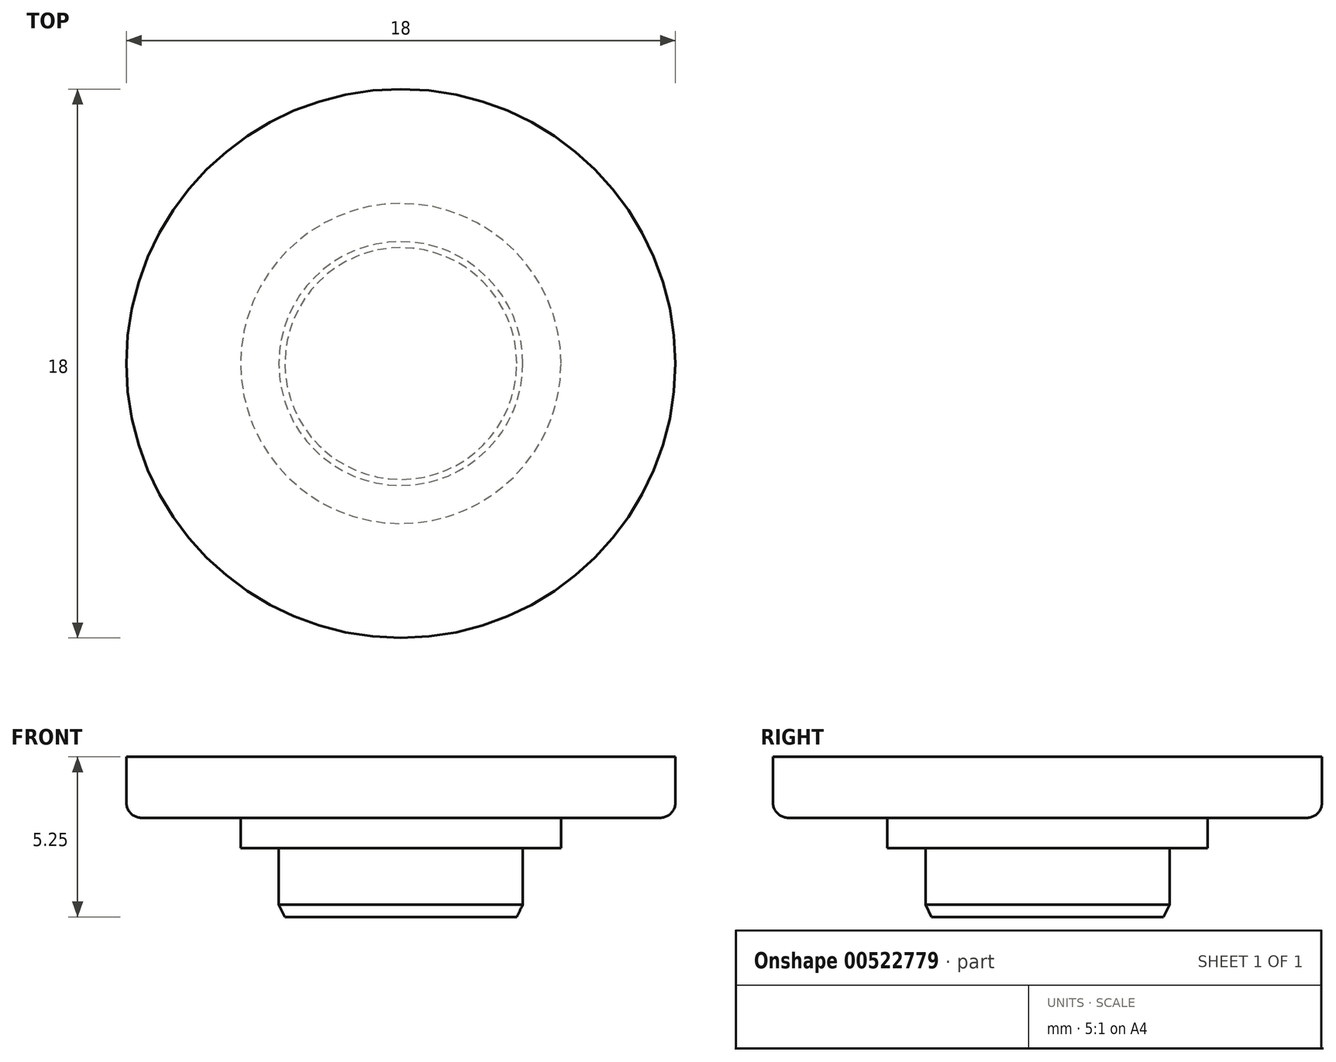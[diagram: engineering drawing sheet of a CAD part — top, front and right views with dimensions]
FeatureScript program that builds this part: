
annotation { "Feature Type Name" : "Feature", "Feature Type Description" : "" }
export const myFeature = defineFeature(function(context is Context, id is Id, definition is map)
    precondition{}
    {
        {
            var Q0;
            Q0=qCreatedBy(makeId("Front.planeOp"),FACE);
            var sketch = newSketch(context, id + "F0", { "sketchPlane" : qUnion([Q0])});
            skLineSegment(sketch, "E0", {"start": v(0, 31.24) * mm, "end": v(0, -31.24) * mm});
            skLineSegment(sketch, "E1", {"start": v(0, -3.25) * mm, "end": v(-4, -3.25) * mm});
            skLineSegment(sketch, "E2", {"start": v(-4, -3.25) * mm, "end": v(-4, -1) * mm});
            skLineSegment(sketch, "E3", {"start": v(-4, -1) * mm, "end": v(-5.25, -1) * mm});
            skLineSegment(sketch, "E4", {"start": v(-5.25, -1) * mm, "end": v(-5.25, 0) * mm});
            skLineSegment(sketch, "E5", {"start": v(-5.25, 0) * mm, "end": v(-9, 0) * mm});
            skLineSegment(sketch, "E6", {"start": v(-9, 0) * mm, "end": v(-9, 2) * mm});
            skLineSegment(sketch, "E7", {"start": v(-9, 2) * mm, "end": v(0, 2) * mm});
            skLineSegment(sketch, "E8", {"start": v(0, 2) * mm, "end": v(0, -3.25) * mm});
            skSolve(sketch);
        }
        {
            var Q0;
            Q0=makeQuery(id+"F0.imprint","IMPRINT",FACE,{"disambiguationData":[TD([[makeQuery(id+"F0.imprint","IMPRINT",EDGE,{"derivedFrom":sQuery(id+"F0.wireOp",EDGE,"E1")}),-1.0]])]});
            var Q1;
            Q1=sQuery(id+"F0.wireOp",EDGE,"E8");
            revolve(context, id + "F1", {"entities" : qUnion([Q0]), "axis" : qUnion([Q1]), "revolveType" : RevolveType.FULL});
        }
        {
            var Q0;
            Q0=makeQuery(id+"F1.opRevolve","SWEPT_EDGE",EDGE,{"disambiguationData":[OSD([sQuery(id+"F0.wireOp",EDGE,"E1"),sQuery(id+"F0.wireOp",EDGE,"E2")])]});
            chamfer(context, id + "F2", {"entities" : qUnion([Q0]), "chamferType" : ChamferType.TWO_OFFSETS, "width1" : .4 * mm, "oppositeDirection" : false, "width2" : .2 * mm, "tangentPropagation" : true});
        }
        {
            var Q0;
            Q0=makeQuery(id+"F1.opRevolve","SWEPT_EDGE",EDGE,{"disambiguationData":[OSD([sQuery(id+"F0.wireOp",EDGE,"E5"),sQuery(id+"F0.wireOp",EDGE,"E6")])]});
            fillet(context, id + "F3", {"entities" : qUnion([Q0]), "radius" : .5 * mm, "tangentPropagation" : true, "allowEdgeOverflow" : false});
        }
    });
